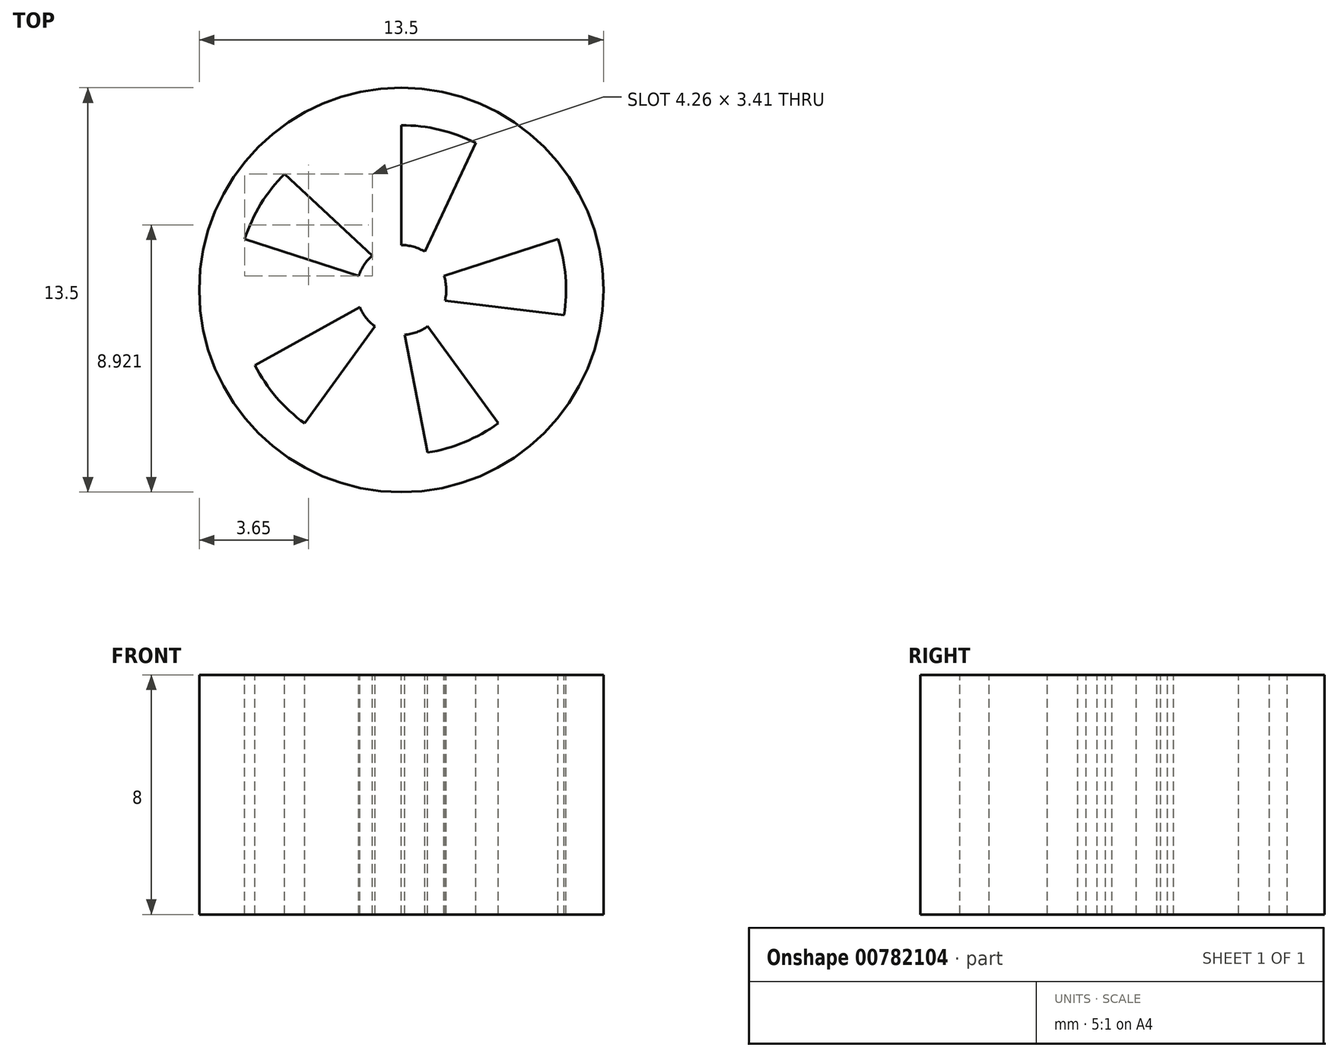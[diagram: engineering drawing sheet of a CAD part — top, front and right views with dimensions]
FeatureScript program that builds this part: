
annotation { "Feature Type Name" : "Feature", "Feature Type Description" : "" }
export const myFeature = defineFeature(function(context is Context, id is Id, definition is map)
    precondition{}
    {
        {
            var Q0;
            Q0=qCreatedBy(makeId("Top.planeOp"),FACE);
            var sketch = newSketch(context, id + "F0", { "sketchPlane" : qUnion([Q0])});
            skCircle(sketch, "E0", {"center": v(0, 0) * mm, "radius": 6.75 * mm});
            skSolve(sketch);
        }
        {
            var Q0;
            Q0=qSketchRegion(id+"F0",true);
            extrude(context, id + "F1", {"entities" : qUnion([Q0]), "depth" : 8 * mm, "offsetDistance" : 25 * mm});
        }
        {
            var Q0;
            Q0=makeQuery(id+"F1.opExtrude","CAP_FACE",FACE,{"disambiguationData":[OSD([sQuery(id+"F0.wireOp",EDGE,"E0")])],"isStart":false});
            var sketch = newSketch(context, id + "F2", { "sketchPlane" : qUnion([Q0])});
            skCircle(sketch, "E1", {"center": v(0, 0) * mm, "radius": 1.5 * mm});
            skCircle(sketch, "E2", {"center": v(0, 0) * mm, "radius": 5.5 * mm});
            skLineSegment(sketch, "E3", {"start": v(0, 1.5) * mm, "end": v(0, 5.5) * mm});
            skLineSegment(sketch, "E4", {"start": v(0.79, 1.28) * mm, "end": v(2.48, 4.9) * mm});
            skLineSegment(sketch, "E5.1.0", {"start": v(-1.43, 0.46) * mm, "end": v(-5.23, 1.7) * mm});
            skLineSegment(sketch, "E5.1.1", {"start": v(-0.97, 1.14) * mm, "end": v(-3.9, 3.88) * mm});
            skLineSegment(sketch, "E5.2.0", {"start": v(-0.88, -1.21) * mm, "end": v(-3.23, -4.45) * mm});
            skLineSegment(sketch, "E5.2.1", {"start": v(-1.39, -0.57) * mm, "end": v(-4.9, -2.51) * mm});
            skLineSegment(sketch, "E5.3.0", {"start": v(0.88, -1.21) * mm, "end": v(3.23, -4.45) * mm});
            skLineSegment(sketch, "E5.3.1", {"start": v(0.11, -1.5) * mm, "end": v(0.88, -5.43) * mm});
            skLineSegment(sketch, "E5.4.0", {"start": v(1.43, 0.46) * mm, "end": v(5.23, 1.7) * mm});
            skLineSegment(sketch, "E5.4.1", {"start": v(1.46, -0.36) * mm, "end": v(5.43, -0.84) * mm});
            skSolve(sketch);
        }
        {
            var Q0;
            {var subQ0=sQuery(id+"F2.wireOp",EDGE,"E3");Q0=makeQuery(id+"F2.imprint","IMPRINT",FACE,{"disambiguationData":[TD([[makeQuery(id+"F2.imprint","IMPRINT",EDGE,{"derivedFrom":subQ0}),-1.0]])]});}
            var Q1;
            {var subQ0=sQuery(id+"F2.wireOp",EDGE,"E5.1.0");Q1=makeQuery(id+"F2.imprint","IMPRINT",FACE,{"disambiguationData":[TD([[makeQuery(id+"F2.imprint","IMPRINT",EDGE,{"derivedFrom":subQ0}),-1.0]])]});}
            var Q2;
            {var subQ0=sQuery(id+"F2.wireOp",EDGE,"E5.2.0");Q2=makeQuery(id+"F2.imprint","IMPRINT",FACE,{"disambiguationData":[TD([[makeQuery(id+"F2.imprint","IMPRINT",EDGE,{"derivedFrom":subQ0}),-1.0]])]});}
            var Q3;
            {var subQ0=sQuery(id+"F2.wireOp",EDGE,"E5.3.0");Q3=makeQuery(id+"F2.imprint","IMPRINT",FACE,{"disambiguationData":[TD([[makeQuery(id+"F2.imprint","IMPRINT",EDGE,{"derivedFrom":subQ0}),-1.0]])]});}
            var Q4;
            {var subQ0=sQuery(id+"F2.wireOp",EDGE,"E5.4.0");Q4=makeQuery(id+"F2.imprint","IMPRINT",FACE,{"disambiguationData":[TD([[makeQuery(id+"F2.imprint","IMPRINT",EDGE,{"derivedFrom":subQ0}),-1.0]])]});}
            extrude(context, id + "F3", {"entities" : qUnion([Q0, Q1, Q2, Q3, Q4]), "operationType" : NewBodyOperationType.REMOVE, "endBound" : BoundingType.THROUGH_ALL, "oppositeDirection" : true, "depth" : 25 * mm, "offsetDistance" : 25 * mm});
        }
    });
